# Revit family: NLRS_57_AIR_UN_rectangular jet diffuser jtga supply LT_sacs
name_source: partatom
category: Air Terminals
revit_build: Autodesk Revit 2018 (Build: 20190510_1515(x64)
units: mm (PartAtom-declared; Revit-internal decimal feet)

## family parameters
Always vertical = Yes
Cut with Voids When Loaded = No
Part Type = Normal
Room Calculation Point = Yes
Round Connector Dimension = Use Diameter
Shared = No
Work Plane-Based = No

## types (16) — shared parameters
Assembly Code = 57.0
Description = Solid Air jet diffuser JTGA (supply)
FactorTable = JTGA_Factors
Jet1_Visible = Yes
LookupTable = JTGA
Manufacturer = Solid Air Climate Systems
Model = Jet diffuser
NLRS_C_content_datum_uitgifte = 03-08-2021
NLRS_C_content_provider = Solid Air Climate Solutions
NLRS_C_content_versie = 3.18.01
NLRS_C_niveau ontwikkeling = LOD 400
SACS_Show_Symbol = No
URL = https://solid-air.nl

## per-type parameters (varying)
| type | Eff_Offset_Jet2 | Eff_Offset_Jet3 | Eff_Offset_Jet4 | Jet2_Visible | Jet3_Visible | Jet4_Visible | Jet_Gaps | Offset_Jet1_to_center | SACS_Array_Count | SACS_Base_Index | SACS_Diameter | SACS_Factor_LpF1 | SACS_Factor_LpF2 | SACS_Factor_PsF1 | SACS_Factor_PsF2 | SACS_Factor_WF1 | SACS_Factor_WF2 | SACS_Height | SACS_Model | SACS_Subindex | SACS_Width |
| JTGAO 160-1 | 1 mm  [stored 0.00328084 ft] | 1 mm  [stored 0.00328084 ft] | 1 mm  [stored 0.00328084 ft] | No | No | No | 0 mm  [stored 0 ft] | 0 mm  [stored 0 ft] | 1 | 1 | 160 mm  [stored 0.524934 ft] | -127.01029 | 26.183073 | 286.689314 | 1.996272 | 0.405084 | 0.55358 | 260 mm  [stored 0.853018 ft] | JTGAOO 160-1 | 1 | 260 mm  [stored 0.853018 ft] |
| JTGAO 160-2 | 244 mm  [stored 0.800525 ft] | 1 mm  [stored 0.00328084 ft] | 1 mm  [stored 0.00328084 ft] | Yes | No | No | 244 mm  [stored 0.800525 ft] | 122 mm  [stored 0.400262 ft] | 2 | 2 | 160 mm  [stored 0.524934 ft] | -140.776806 | 25.986197 | 70.87589 | 2.002378 | 0.427101 | 0.521996 | 260 mm  [stored 0.853018 ft] | JTGAOO 160-2 | 1 | 505 mm  [stored 1.65682 ft] |
| JTGAO 160-3 | 244 mm  [stored 0.800525 ft] | 244 mm  [stored 0.800525 ft] | 1 mm  [stored 0.00328084 ft] | Yes | Yes | No | 244 mm  [stored 0.800525 ft] | 244 mm  [stored 0.800525 ft] | 3 | 3 | 160 mm  [stored 0.524934 ft] | -151.209215 | 26.264194 | 31.983754 | 2.001706 | 0.345025 | 0.53954 | 260 mm  [stored 0.853018 ft] | JTGAOO 160-3 | 1 | 750 mm  [stored 2.46063 ft] |
| JTGAO 160-4 | 244 mm  [stored 0.800525 ft] | 244 mm  [stored 0.800525 ft] | 244 mm  [stored 0.800525 ft] | Yes | Yes | Yes | 244 mm  [stored 0.800525 ft] | 366 mm  [stored 1.20079 ft] | 4 | 4 | 160 mm  [stored 0.524934 ft] | -156.536784 | 26.124488 | 17.963416 | 2.002232 | 0.205421 | 0.597156 | 260 mm  [stored 0.853018 ft] | JTGAOO 160-4 | 1 | 995 mm  [stored 3.26444 ft] |
| JTGAO 200-1 | 1 mm  [stored 0.00328084 ft] | 1 mm  [stored 0.00328084 ft] | 1 mm  [stored 0.00328084 ft] | No | No | No | 0 mm  [stored 0 ft] | 0 mm  [stored 0 ft] | 1 | 5 | 200 mm  [stored 0.656168 ft] | -132.764373 | 25.83909 | 139.455855 | 1.997527 | 0.336906 | 0.568318 | 310 mm  [stored 1.01706 ft] | JTGAOO 200-1 | 2 | 310 mm  [stored 1.01706 ft] |
| JTGAO 200-2 | 294 mm  [stored 0.964567 ft] | 1 mm  [stored 0.00328084 ft] | 1 mm  [stored 0.00328084 ft] | Yes | No | No | 294 mm  [stored 0.964567 ft] | 147 mm  [stored 0.482283 ft] | 2 | 6 | 200 mm  [stored 0.656168 ft] | -148.667479 | 25.989958 | 33.595579 | 2.005019 | 0.300865 | 0.557898 | 310 mm  [stored 1.01706 ft] | JTGAOO 200-2 | 2 | 605 mm  [stored 1.98491 ft] |
| JTGAO 200-3 | 294 mm  [stored 0.964567 ft] | 294 mm  [stored 0.964567 ft] | 1 mm  [stored 0.00328084 ft] | Yes | Yes | No | 294 mm  [stored 0.964567 ft] | 294 mm  [stored 0.964567 ft] | 3 | 7 | 200 mm  [stored 0.656168 ft] | -158.75281 | 26.20691 | 15.667233 | 1.999929 | 0.166488 | 0.621855 | 310 mm  [stored 1.01706 ft] | JTGAOO 200-3 | 2 | 900 mm  [stored 2.95276 ft] |
| JTGAO 200-4 | 294 mm  [stored 0.964567 ft] | 294 mm  [stored 0.964567 ft] | 294 mm  [stored 0.964567 ft] | Yes | Yes | Yes | 294 mm  [stored 0.964567 ft] | 441 mm  [stored 1.44685 ft] | 4 | 8 | 200 mm  [stored 0.656168 ft] | -165.039679 | 26.174881 | 8.373404 | 2.006095 | 0.128284 | 0.643238 | 310 mm  [stored 1.01706 ft] | JTGAOO 200-4 | 2 | 1195 mm  [stored 3.9206 ft] |
| JTGAO 250-1 | 1 mm  [stored 0.00328084 ft] | 1 mm  [stored 0.00328084 ft] | 1 mm  [stored 0.00328084 ft] | No | No | No | 0 mm  [stored 0 ft] | 0 mm  [stored 0 ft] | 1 | 9 | 250 mm  [stored 0.82021 ft] | -146.642993 | 26.17929 | 46.052769 | 1.998901 | 0.320699 | 0.55396 | 360 mm  [stored 1.1811 ft] | JTGAOO 250-1 | 3 | 360 mm  [stored 1.1811 ft] |
| JTGAO 250-2 | 344 mm  [stored 1.12861 ft] | 1 mm  [stored 0.00328084 ft] | 1 mm  [stored 0.00328084 ft] | Yes | No | No | 344 mm  [stored 1.12861 ft] | 172 mm  [stored 0.564304 ft] | 2 | 10 | 250 mm  [stored 0.82021 ft] | -161.591113 | 26.125945 | 11.991115 | 1.992521 | 0.193575 | 0.596745 | 360 mm  [stored 1.1811 ft] | JTGAOO 250-2 | 3 | 705 mm  [stored 2.31299 ft] |
| JTGAO 250-3 | 344 mm  [stored 1.12861 ft] | 344 mm  [stored 1.12861 ft] | 1 mm  [stored 0.00328084 ft] | Yes | Yes | No | 344 mm  [stored 1.12861 ft] | 344 mm  [stored 1.12861 ft] | 3 | 11 | 250 mm  [stored 0.82021 ft] | -167.612703 | 25.765327 | 5.068172 | 1.999272 | 0.085926 | 0.682477 | 360 mm  [stored 1.1811 ft] | JTGAOO 250-3 | 3 | 1050 mm  [stored 3.44488 ft] |
| JTGAO 250-4 | 344 mm  [stored 1.12861 ft] | 344 mm  [stored 1.12861 ft] | 344 mm  [stored 1.12861 ft] | Yes | Yes | Yes | 344 mm  [stored 1.12861 ft] | 516 mm | 4 | 12 | 250 mm  [stored 0.82021 ft] | -177.912767 | 26.296238 | 2.88511 | 1.998742 | 0.065987 | 0.700992 | 360 mm  [stored 1.1811 ft] | JTGAOO 250-4 | 3 | 1395 mm  [stored 4.57677 ft] |
| JTGAO 315-1 | 1 mm  [stored 0.00328084 ft] | 1 mm  [stored 0.00328084 ft] | 1 mm  [stored 0.00328084 ft] | No | No | No | 0 mm  [stored 0 ft] | 0 mm  [stored 0 ft] | 1 | 13 | 315 mm  [stored 1.03346 ft] | -155.789065 | 25.986197 | 17.342842 | 1.995663 | 0.169358 | 0.621763 | 410 mm  [stored 1.34514 ft] | JTGAOO 315-1 | 4 | 410 mm  [stored 1.34514 ft] |
| JTGAO 315-2 | 394 mm  [stored 1.29265 ft] | 1 mm  [stored 0.00328084 ft] | 1 mm  [stored 0.00328084 ft] | Yes | No | No | 394 mm  [stored 1.29265 ft] | 197 mm | 2 | 14 | 315 mm  [stored 1.03346 ft] | -172.060965 | 26.152018 | 4.14278 | 2.00054 | 0.095904 | 0.665278 | 410 mm  [stored 1.34514 ft] | JTGAOO 315-2 | 4 | 805 mm  [stored 2.64108 ft] |
| JTGAO 315-3 | 394 mm  [stored 1.29265 ft] | 394 mm  [stored 1.29265 ft] | 1 mm  [stored 0.00328084 ft] | Yes | Yes | No | 394 mm  [stored 1.29265 ft] | 394 mm  [stored 1.29265 ft] | 3 | 15 | 315 mm  [stored 1.03346 ft] | -178.127237 | 25.795934 | 1.790442 | 2.003661 | 0.046091 | 0.734848 | 410 mm  [stored 1.34514 ft] | JTGAOO 315-3 | 4 | 1200 mm  [stored 3.93701 ft] |
| JTGAO 315-4 | 394 mm  [stored 1.29265 ft] | 394 mm  [stored 1.29265 ft] | 394 mm  [stored 1.29265 ft] | Yes | Yes | Yes | 394 mm  [stored 1.29265 ft] | 591 mm | 4 | 16 | 315 mm  [stored 1.03346 ft] | -186.879327 | 26.125587 | 1.117231 | 1.993646 | 0.031192 | 0.766756 | 410 mm  [stored 1.34514 ft] | JTGAOO 315-4 | 4 | 1595 mm  [stored 5.23294 ft] |

note: [stored X ft] marks values corroborated as IEEE doubles in the binary element streams (Revit-internal decimal feet)

## geometry (parser evidence)
native form markers: Sweep x18
no freeform markers — native parametric forms only
